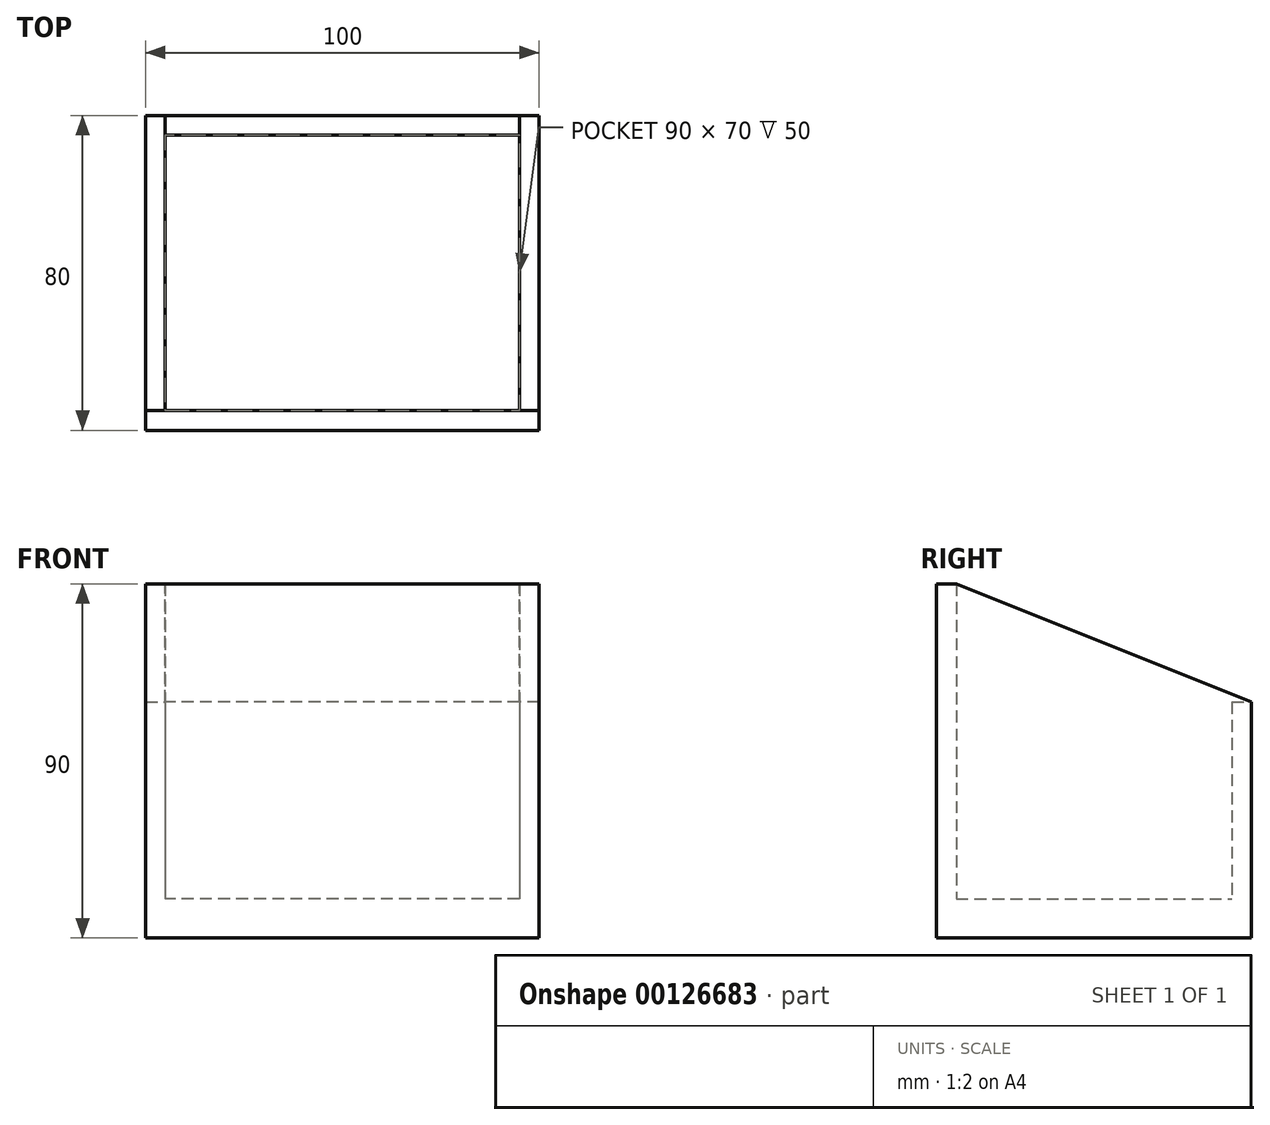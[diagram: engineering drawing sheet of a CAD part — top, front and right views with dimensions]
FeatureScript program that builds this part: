
annotation { "Feature Type Name" : "Feature", "Feature Type Description" : "" }
export const myFeature = defineFeature(function(context is Context, id is Id, definition is map)
    precondition{}
    {
        {
            var Q0;
            Q0=qCreatedBy(makeId("Top.planeOp"),FACE);
            var sketch = newSketch(context, id + "F0", { "sketchPlane" : qUnion([Q0])});
            skLineSegment(sketch, "E0.bottom", {"start": v(50, -40) * mm, "end": v(-50, -40) * mm});
            skLineSegment(sketch, "E0.top", {"start": v(50, 40) * mm, "end": v(-50, 40) * mm});
            skLineSegment(sketch, "E0.left", {"start": v(50, -40) * mm, "end": v(50, 40) * mm});
            skLineSegment(sketch, "E0.right", {"start": v(-50, -40) * mm, "end": v(-50, 40) * mm});
            skPoint(sketch, "E0.middle", {"position": v(0, 0) * mm});
            skLineSegment(sketch, "E1.bottom", {"start": v(45, -35) * mm, "end": v(-45, -35) * mm});
            skLineSegment(sketch, "E1.top", {"start": v(45, 35) * mm, "end": v(-45, 35) * mm});
            skLineSegment(sketch, "E1.left", {"start": v(45, -35) * mm, "end": v(45, 35) * mm});
            skLineSegment(sketch, "E1.right", {"start": v(-45, -35) * mm, "end": v(-45, 35) * mm});
            skLineSegment(sketch, "E2", {"start": v(-45, -35) * mm, "end": v(-50, -35) * mm});
            skLineSegment(sketch, "E3", {"start": v(-50, -35) * mm, "end": v(50, -35) * mm});
            skSolve(sketch);
        }
        {
            var Q0;
            {var subQ1=sQuery(id+"F0.wireOp",EDGE,"E0.top");Q0=makeQuery(id+"F0.imprint","IMPRINT",FACE,{"disambiguationData":[TD([[makeQuery(id+"F0.imprint","IMPRINT",EDGE,{"derivedFrom":subQ1}),1.0]])]});}
            extrude(context, id + "F1", {"entities" : qUnion([Q0]), "depth" : 60 * mm});
        }
        {
            var Q0;
            Q0=makeQuery(id+"F0.imprint","IMPRINT",FACE,{"disambiguationData":[TD([[makeQuery(id+"F0.imprint","IMPRINT",EDGE,{"derivedFrom":sQuery(id+"F0.wireOp",EDGE,"E1.top")}),1.0]])]});
            extrude(context, id + "F2", {"entities" : qUnion([Q0]), "operationType" : NewBodyOperationType.ADD, "depth" : 10 * mm});
        }
        {
            var Q0;
            {var subQ5=sQuery(id+"F0.wireOp",EDGE,"E0.bottom");Q0=makeQuery(id+"F0.imprint","IMPRINT",FACE,{"disambiguationData":[TD([[makeQuery(id+"F0.imprint","IMPRINT",EDGE,{"derivedFrom":subQ5}),-1.0]])]});}
            extrude(context, id + "F3", {"entities" : qUnion([Q0]), "operationType" : NewBodyOperationType.ADD, "depth" : 90 * mm});
        }
        {
            var Q0;
            Q0=qCreatedBy(makeId("Right.planeOp"),FACE);
            var sketch = newSketch(context, id + "F4", { "sketchPlane" : qUnion([Q0])});
            skLineSegment(sketch, "E4", {"start": v(-35.3, 60) * mm, "end": v(40, 60) * mm});
            skLineSegment(sketch, "E5", {"start": v(40, 60) * mm, "end": v(-35.03, 89.99) * mm});
            skLineSegment(sketch, "E6", {"start": v(-35.03, 89.99) * mm, "end": v(-35.3, 60) * mm});
            skSolve(sketch);
        }
        {
            var Q0;
            Q0=makeQuery(id+"F4.imprint","IMPRINT",FACE,{"disambiguationData":[TD([[makeQuery(id+"F4.imprint","IMPRINT",EDGE,{"derivedFrom":sQuery(id+"F4.wireOp",EDGE,"E4")}),1.0]])]});
            extrude(context, id + "F5", {"entities" : qUnion([Q0]), "operationType" : NewBodyOperationType.ADD, "depth" : 50 * mm, "hasSecondDirection" : true, "secondDirectionOppositeDirection" : false, "secondDirectionDepth" : 45 * mm});
        }
        {
            var Q0;
            Q0 = qSketchRegion(id + "F4", true);
            extrude(context, id + "F6", {"entities" : qUnion([Q0]), "operationType" : NewBodyOperationType.ADD, "oppositeDirection" : true, "depth" : 50 * mm, "hasSecondDirection" : true, "secondDirectionOppositeDirection" : true, "secondDirectionDepth" : 45 * mm});
        }
    });
